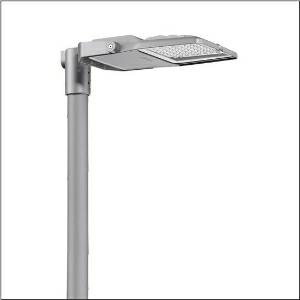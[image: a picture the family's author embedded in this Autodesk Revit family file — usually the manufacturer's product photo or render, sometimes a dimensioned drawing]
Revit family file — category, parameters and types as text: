
# Revit family: floodlight_fl_21_iq_mini___pl33t_5xa7772c2f3a_076b
name_source: partatom
category: Lighting Fixtures
units: mm (PartAtom-declared; Revit-internal decimal feet)

## family parameters
Cut with Voids When Loaded = No
Host = Face
Light Source = No
Part Type = Normal
Room Calculation Point = No
Round Connector Dimension = Use Diameter
Shared = No

## types (1)
- --- (1 x LED, 12060 lm, 87.2 W, 3000K)
    Apparent Load = 87 VA
    CIE Flux Codes = 26 75 99 100 100
    Color Rendering = 70
    Color Temperature = 3000K
    Default Elevation = 1800 mm
    Description = Floodlight FL 21 iQ mini, floodlight, primary light control with lens, of PMMA, primary optical cover: protective disc, of toughened safety glass, transparent, light distribution: PL33T, light emission: direct distribution, installation type: surface-mounted, LED, High Power LED, rated luminous flux: 12.060lm, luminous efficacy: 138lm/W, light colour: 730, colour temperature: 3000K, control gear: iQ Street-Remote/DALI, control: Auto-Match, Temp-Guard, Night-Set, Smart-Wire, Desk-Remote (wireless, voltage-free reading and setting of iQ features in the workshop via application-optimized NFC function/RFID function), optimised constant luminous flux control (CLO 2.0), Light-Fading, Lumen-Switch, with terminal, 6-pole, mains connection: 220..240V, AC, 50/60Hz, start of lifetime: 87W, end of service life: 92W, reduction: 40W, luminaire housing, of diecast aluminium, powder-coated, Siteco® metallic grey (DB 702S), corrosivity category C5 mid according to DIN EN ISO 12944, suitable for swimming pools, chlorine-resistant, sealing non-destructively replaceable, please order mast flange separately, mast bracket, of steel, galvanised, powder-coated, protection rating (complete): IP66, insulation class (complete): insulation class II (safety insulation), certification: CE, ENEC, VDE, protection symbol: D, impact resistance: IK08, permissible operating ambient temperature: -40..+40°C, permissible operating ambient temperature for outdoor applications: -40..+50°C, standard: DIN EN 12944, LABS conformity tested according to VDMA 24364:2018-05, packaging unit: 1 piece

Light Distribution: PL33T
    Height = 70 mm
    Lamp = 1 x LED
    Lamp Light Flux = 12060 lm
    Lamp Power = 87.2 W
    Lamp count = 1
    Length = 485 mm
    Luminous efficacy = 138 lm/W
    Manufacturer = Siteco
    ModVariant = No
    Model = 5XA7772C2F3A
    Number of Poles = 1
    OnlyDefault = Yes
    Power Factor = 1
    Product Name = Floodlight FL 21 iQ mini | PL33T
    Product group = floodlight | pylon annexe
    ProductGroupID = 6201
    Protection Class = Protection class II
    Protection Degree = IP 66
    RLX_Detail_Level = 1
    RLX_Emergency_Light_Flux = 0 lm
    RLX_Emergency_Type = 0
    RLX_Emergency_Type_DB = No
    RlxData = <blob elided: 101365 chars, md5=0abc588a>
    Socket = socket
    Standby Power = 0 W
    System Light Flux = 12060 lm
    System Power = 87 W
    Type Comments = factory setting: luminous flux: 100 % | dim-lin: 254 | 456 mA
    Type Image = l_1007125.jpg
    URL = http://relux.com
    VarID = @adj_170933
    Voltage = 0 V
    Weight = 0.00 kg
    Width = 337 mm

## geometry (parser evidence)
native form markers: Blend x4, Sweep x13
no freeform markers — native parametric forms only
